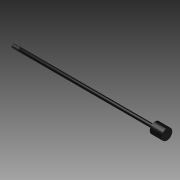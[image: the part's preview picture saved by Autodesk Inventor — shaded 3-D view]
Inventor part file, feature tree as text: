
AUTODESK INVENTOR PART (.ipt)
format: ipt  version: 2011 SP1 (Build 150282100, 282)  size: 118,272 bytes
history: native  units: in
note: dims shown in document units (in); Inventor stores cm internally (conversion verified against a paired STEP export)
features: other x70, revolve x3, sketch x3, thread x1
ambient origin geometry x8: Origin, YZ Plane, XZ Plane, XY Plane, X Axis, Y Axis, Z Axis, Center Point
bodies: Solid1 (feature_tree)
feature tree (77):
  revolve  "Revolution1"  Angle=360.0deg
  revolve  "Revolution2"  Angle=360.0deg
  thread  "Thread1"  [1 undecoded]
  revolve  "Revolution3"  [1 undecoded]
  other  "dia1_XY"
  other  "dia1_YZ"
  other  "dia1_ZX"
  other  "dia1_X"
  other  "dia1_Y"
  other  "dia1_Z"
  other  "dia1_Center"
  other  "dia12_XY"
  other  "dia12_YZ"
  other  "dia12_ZX"
  other  "dia12_X"
  other  "dia12_Y"
  other  "dia12_Z"
  other  "dia12_Center"
  other  "dia2_XY"
  other  "dia2_YZ"
  other  "dia2_ZX"
  other  "dia2_X"
  other  "dia2_Y"
  other  "dia2_Z"
  other  "dia2_Center"
  other  "dia22_XY"
  other  "dia22_YZ"
  other  "dia22_ZX"
  other  "dia22_X"
  other  "dia22_Y"
  other  "dia22_Z"
  other  "dia22_Center"
  other  "rl1_XY"
  other  "rl1_YZ"
  other  "rl1_ZX"
  other  "rl1_X"
  other  "rl1_Y"
  other  "rl1_Z"
  other  "rl1_Center"
  other  "rl2_XY"
  other  "rl2_YZ"
  other  "rl2_ZX"
  other  "rl2_X"
  other  "rl2_Y"
  other  "rl2_Z"
  other  "rl2_Center"
  other  "rod_cp_XY"
  other  "rod_cp_YZ"
  other  "rod_cp_ZX"
  other  "rod_cp_X"
  other  "rod_cp_Y"
  other  "rod_cp_Z"
  other  "rod_cp_Center"
  other  "thd1_XY"
  other  "thd1_YZ"
  other  "thd1_ZX"
  other  "thd1_X"
  other  "thd1_Y"
  other  "thd1_Z"
  other  "thd1_Center"
  other  "thd2_XY"
  other  "thd2_YZ"
  other  "thd2_ZX"
  other  "thd2_X"
  other  "thd2_Y"
  other  "thd2_Z"
  other  "thd2_Center"
  other  "to_rod_clevis_XY"
  other  "to_rod_clevis_YZ"
  other  "to_rod_clevis_ZX"
  other  "to_rod_clevis_X"
  other  "to_rod_clevis_Y"
  other  "to_rod_clevis_Z"
  other  "to_rod_clevis_Center"
  sketch  "Sketch_1"  dims[d0=360.0deg d1=360.0deg]
  sketch  "Sketch_3"  dims[d2=0.4787in d3=0.0in d4=360.0deg d5=0.0in d6=0.0in d7=0.0in]
  sketch  "Sketch_30"
note: 2 required parameter values undecoded (feature->parameter linkage not recoverable at this tier; creation-order binding heuristic only, values carry confidence <= 0.55)
